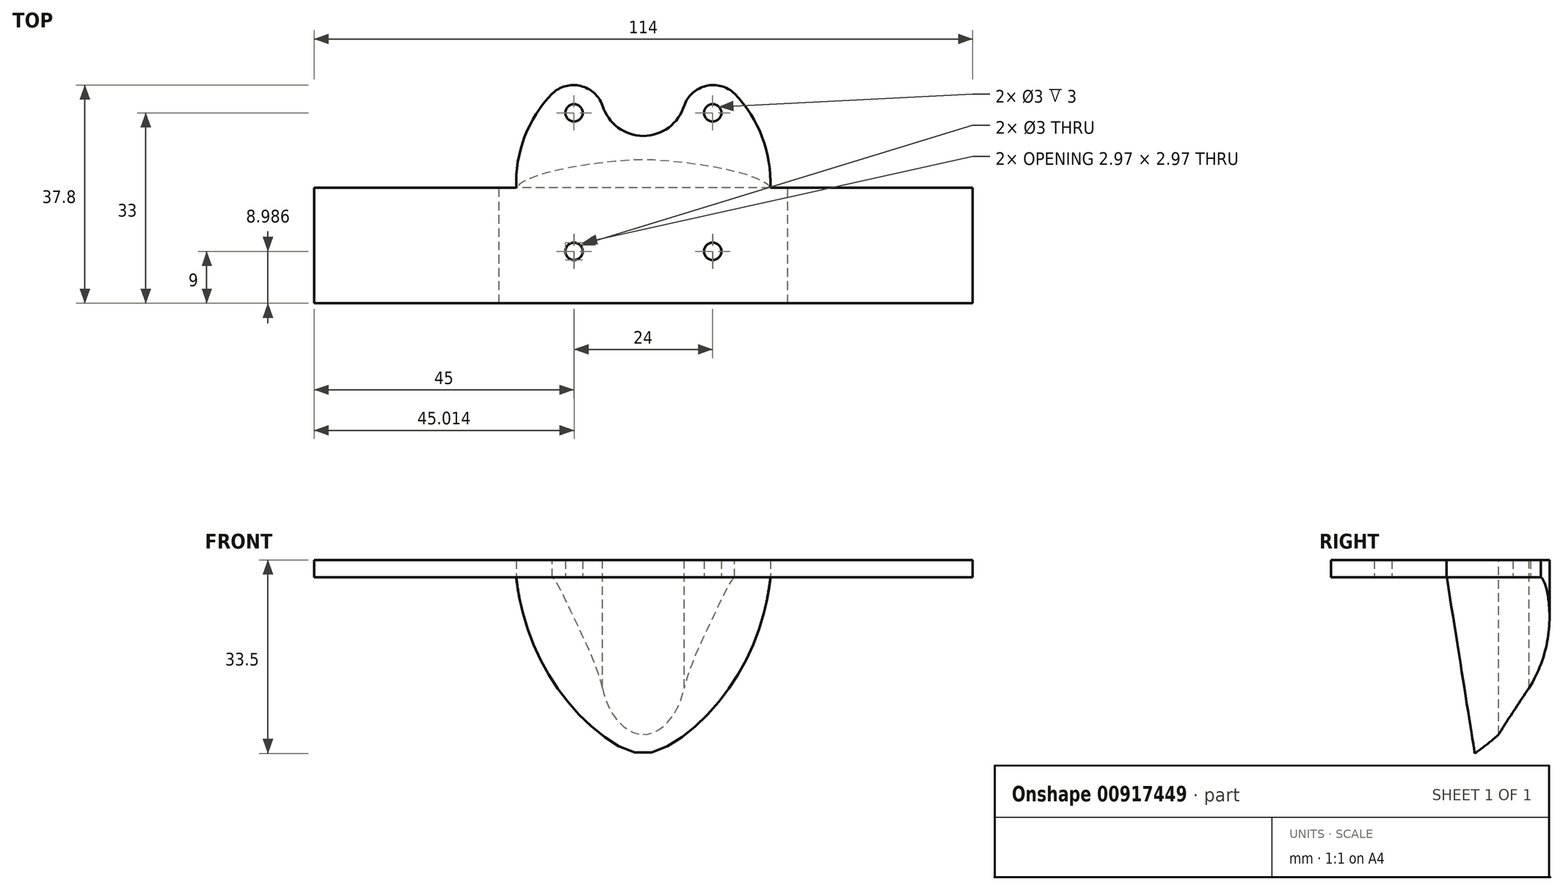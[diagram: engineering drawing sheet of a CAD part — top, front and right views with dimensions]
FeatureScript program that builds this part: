
annotation { "Feature Type Name" : "Feature", "Feature Type Description" : "" }
export const myFeature = defineFeature(function(context is Context, id is Id, definition is map)
    precondition{}
    {
        {
            var Q0;
            Q0=qCreatedBy(makeId("Top.planeOp"),FACE);
            var sketch = newSketch(context, id + "F0", { "sketchPlane" : qUnion([Q0])});
            skLineSegment(sketch, "E0.bottom", {"start": v(57, -21) * mm, "end": v(6.56, -21) * mm});
            skLineSegment(sketch, "E0.top", {"start": v(57, -1) * mm, "end": v(21.98, -1) * mm});
            skLineSegment(sketch, "E0.left", {"start": v(57, -21) * mm, "end": v(57, -1) * mm});
            skLineSegment(sketch, "E0.right", {"start": v(-57, -21) * mm, "end": v(-57, -1) * mm});
            skCircle(sketch, "E1", {"center": v(-12, 12) * mm, "radius": 1.5 * mm});
            skCircle(sketch, "E2", {"center": v(12, 12) * mm, "radius": 1.5 * mm});
            skCircle(sketch, "E3", {"center": v(12, -12) * mm, "radius": 1.5 * mm});
            skCircle(sketch, "E4", {"center": v(-12, -12) * mm, "radius": 1.5 * mm});
            skLineSegment(sketch, "E5", {"start": v(6.56, -21) * mm, "end": v(6.56, -21) * mm});
            skArc(sketch, "E6.trimOffspring", {"start": v(21.98, -1) * mm, "mid": v(0, 22) * mm, "end": v(-21.98, -1) * mm});
            skLineSegment(sketch, "E7.trimOffspring", {"start": v(-21.98, -1) * mm, "end": v(-57, -1) * mm});
            skLineSegment(sketch, "E8.trimOffspring", {"start": v(6.56, -21) * mm, "end": v(-57, -21) * mm});
            skSolve(sketch);
        }
        {
            var Q0;
            Q0 = qSketchRegion(id + "F0", true);
            extrude(context, id + "F1", {"entities" : qUnion([Q0]), "depth" : 3 * mm, "offsetDistance" : 25 * mm});
        }
        {
            var Q0;
            Q0=qCreatedBy(makeId("Right.planeOp"),FACE);
            var sketch = newSketch(context, id + "F2", { "sketchPlane" : qUnion([Q0])});
            skArc(sketch, "E9", {"start": v(0, -32.88) * mm, "mid": v(15.03, -19.14) * mm, "end": v(22, 0) * mm});
            skLineSegment(sketch, "E10", {"start": v(0, 0) * mm, "end": v(22, 0) * mm});
            skLineSegment(sketch, "E11", {"start": v(0, 0) * mm, "end": v(0, -32.88) * mm});
            skSolve(sketch);
        }
        {
            var Q0;
            {var subQ0=sQuery(id+"F2.wireOp",EDGE,"E9");Q0=makeQuery(id+"F2.imprint","IMPRINT",FACE,{"disambiguationData":[TD([[makeQuery(id+"F2.imprint","IMPRINT",EDGE,{"derivedFrom":subQ0}),1.0]])]});}
            var Q1;
            Q1 = qSketchRegion(id + "F4", true);
            var Q2;
            Q2=sQuery(id+"F2.wireOp",EDGE,"E11");
            revolve(context, id + "F3", {"operationType" : NewBodyOperationType.ADD, "surfaceOperationType" : NewSurfaceOperationType.NEW, "entities" : qUnion([Q0, Q1]), "axis" : qUnion([Q2]), "revolveType" : RevolveType.FULL});
        }
        {
            var Q0;
            Q0=qCreatedBy(makeId("Right.planeOp"),FACE);
            var sketch = newSketch(context, id + "F4", { "sketchPlane" : qUnion([Q0])});
            skLineSegment(sketch, "E12", {"start": v(-0.98, 0.05) * mm, "end": v(7.2, -51.62) * mm});
            skLineSegment(sketch, "E13", {"start": v(7.2, -51.62) * mm, "end": v(-21.72, -52.2) * mm});
            skLineSegment(sketch, "E14", {"start": v(-21.72, -52.2) * mm, "end": v(-22.75, 0) * mm});
            skLineSegment(sketch, "E15", {"start": v(-22.75, 0) * mm, "end": v(-0.98, 0.05) * mm});
            skSolve(sketch);
        }
        {
            var Q0;
            Q0 = qSketchRegion(id + "F4", true);
            extrude(context, id + "F5", {"entities" : qUnion([Q0]), "operationType" : NewBodyOperationType.REMOVE, "depth" : 50 * mm, "offsetDistance" : 25 * mm, "symmetric" : true});
        }
        {
            var Q0;
            Q0=makeQuery(id+"F1.opExtrude","CAP_FACE",FACE,{"disambiguationData":[OSD([sQuery(id+"F0.wireOp",EDGE,"E0.bottom"),sQuery(id+"F0.wireOp",EDGE,"E0.top"),sQuery(id+"F0.wireOp",EDGE,"E0.left"),sQuery(id+"F0.wireOp",EDGE,"E0.right"),sQuery(id+"F0.wireOp",EDGE,"E1"),sQuery(id+"F0.wireOp",EDGE,"E2"),sQuery(id+"F0.wireOp",EDGE,"E3"),sQuery(id+"F0.wireOp",EDGE,"E4"),sQuery(id+"F0.wireOp",EDGE,"E6.trimOffspring"),sQuery(id+"F0.wireOp",EDGE,"E7.trimOffspring"),sQuery(id+"F0.wireOp",EDGE,"E8.trimOffspring")])],"isStart":false});
            var sketch = newSketch(context, id + "F6", { "sketchPlane" : qUnion([Q0])});
            skCircle(sketch, "E16.0", {"center": v(-12, 12) * mm, "radius": 1.5 * mm});
            skCircle(sketch, "E16.1", {"center": v(12, -12) * mm, "radius": 1.5 * mm});
            skCircle(sketch, "E16.2", {"center": v(12, 12) * mm, "radius": 1.5 * mm});
            skCircle(sketch, "E16.3", {"center": v(-12, -12) * mm, "radius": 1.5 * mm});
            skArc(sketch, "E17", {"start": v(-7.16, 13.62) * mm, "mid": v(-0.19, 8) * mm, "end": v(7.06, 13.26) * mm});
            skArc(sketch, "E18", {"start": v(15.79, 15.32) * mm, "mid": v(10.87, 16.66) * mm, "end": v(7.06, 13.26) * mm});
            skArc(sketch, "E19.MirrorCS", {"start": v(-15.79, 15.32) * mm, "mid": v(-10.87, 16.66) * mm, "end": v(-7.06, 13.26) * mm});
            skArc(sketch, "E20", {"start": v(15.79, 15.32) * mm, "mid": v(0, 22.04) * mm, "end": v(-15.79, 15.32) * mm});
            skSolve(sketch);
        }
        {
            var Q0;
            {var subQ1=sQuery(id+"F6.wireOp",EDGE,"E17");var subQ6=sQuery(id+"F6.wireOp",EDGE,"WDheHJFC-jQN2-XGF9-Hd2n-fxOeylIydy2h");var subQ8=makeQuery(id+"F6.imprint","INTERSECT",VERTEX,{"disambiguationData":[OD(1.0)],"derivedFrom":[subQ1,subQ6]});Q0=makeQuery(id+"F6.imprint","IMPRINT",FACE,{"disambiguationData":[TD([[makeQuery(id+"F6.imprint","IMPRINT",EDGE,{"disambiguationData":[TD([[subQ8,1.0]])],"derivedFrom":subQ1}),1.0]])]});}
            extrude(context, id + "F7", {"entities" : qUnion([Q0]), "operationType" : NewBodyOperationType.REMOVE, "oppositeDirection" : true, "depth" : 35 * mm, "offsetDistance" : 25 * mm});
        }
    });
